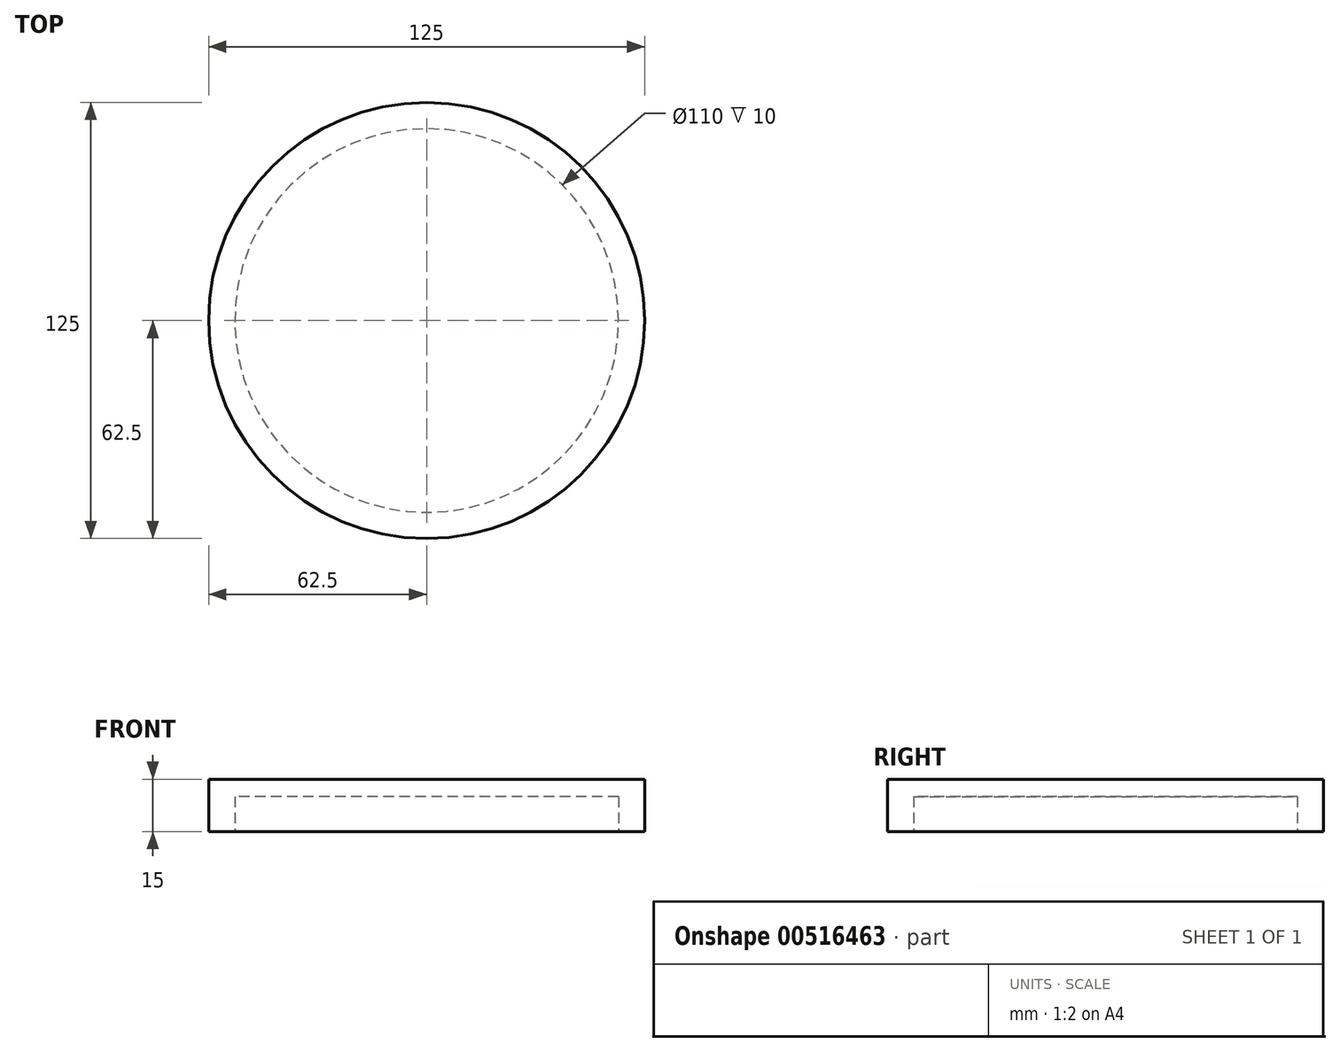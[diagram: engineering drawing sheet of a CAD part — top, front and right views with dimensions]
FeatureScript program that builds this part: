
annotation { "Feature Type Name" : "Feature", "Feature Type Description" : "" }
export const myFeature = defineFeature(function(context is Context, id is Id, definition is map)
    precondition{}
    {
        {
            var Q0;
            Q0=qCreatedBy(makeId("Top.planeOp"),FACE);
            var sketch = newSketch(context, id + "F0", { "sketchPlane" : qUnion([Q0])});
            skCircle(sketch, "E0", {"center": v(0, 0) * mm, "radius": 62.5 * mm});
            skSolve(sketch);
        }
        {
            var Q0;
            Q0=makeQuery(id+"F0.imprint","IMPRINT",FACE,{"disambiguationData":[TD([[makeQuery(id+"F0.imprint","IMPRINT",EDGE,{"derivedFrom":sQuery(id+"F0.wireOp",EDGE,"E0")}),1.0]])]});
            extrude(context, id + "F1", {"entities" : qUnion([Q0]), "depth" : 15 * mm, "offsetDistance" : 25 * mm});
        }
        {
            var Q0;
            Q0=qCreatedBy(makeId("Top.planeOp"),FACE);
            var sketch = newSketch(context, id + "F2", { "sketchPlane" : qUnion([Q0])});
            skCircle(sketch, "E1", {"center": v(0, 0) * mm, "radius": 55 * mm});
            skSolve(sketch);
        }
        {
            var Q0;
            Q0=makeQuery(id+"F2.imprint","IMPRINT",FACE,{"disambiguationData":[TD([[makeQuery(id+"F2.imprint","IMPRINT",EDGE,{"derivedFrom":sQuery(id+"F2.wireOp",EDGE,"E1")}),1.0]])]});
            extrude(context, id + "F3", {"entities" : qUnion([Q0]), "operationType" : NewBodyOperationType.REMOVE, "depth" : 10 * mm, "offsetDistance" : 25 * mm});
        }
    });
